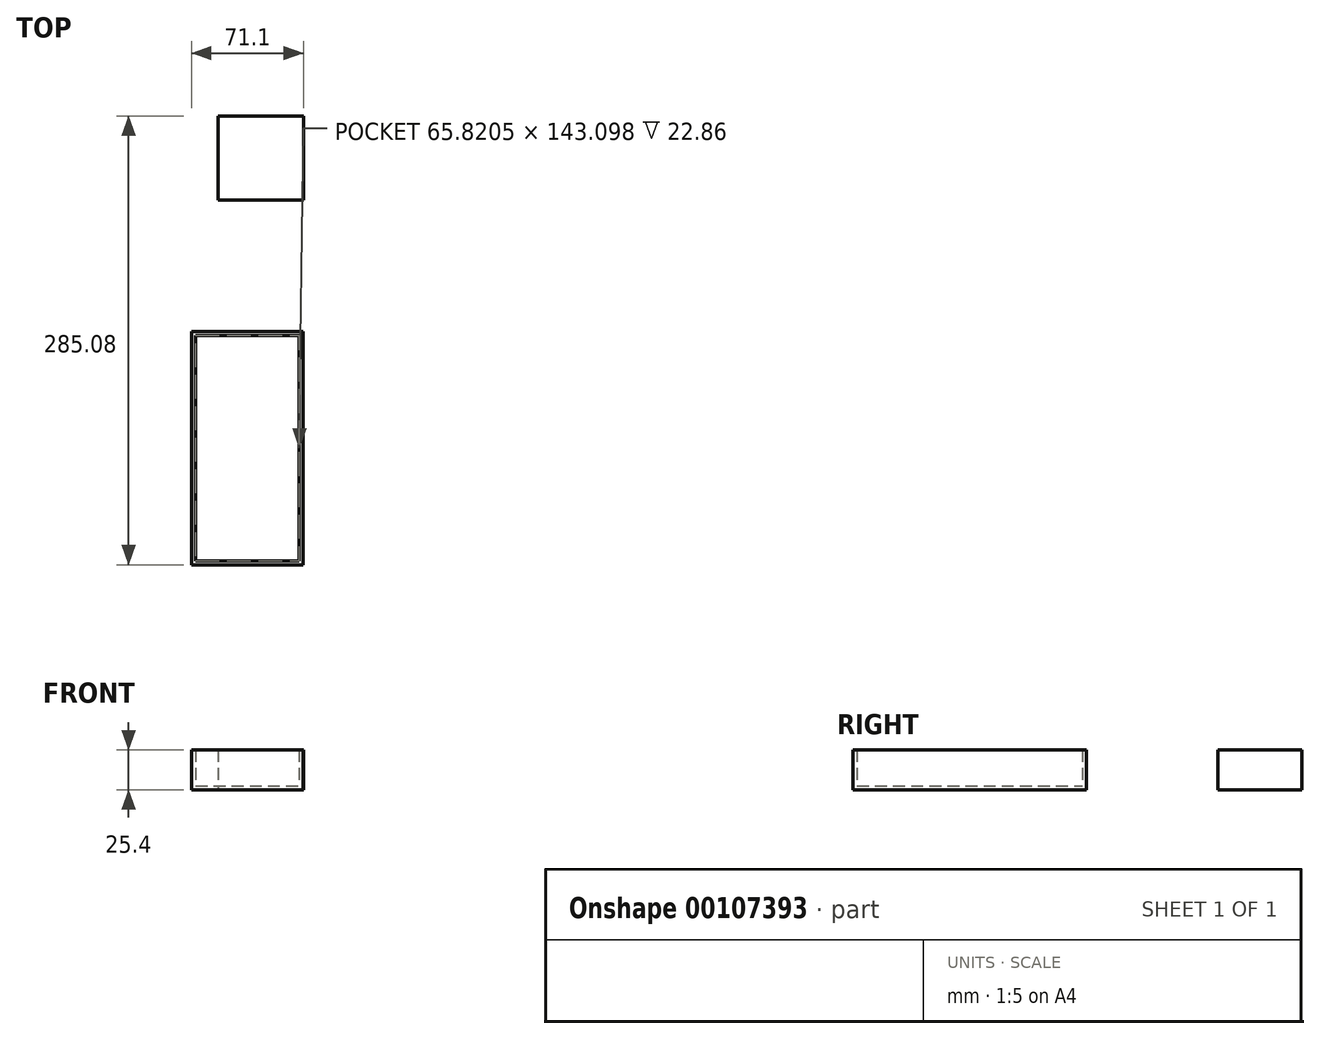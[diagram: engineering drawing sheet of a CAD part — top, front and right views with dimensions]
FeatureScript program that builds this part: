
annotation { "Feature Type Name" : "Feature", "Feature Type Description" : "" }
export const myFeature = defineFeature(function(context is Context, id is Id, definition is map)
    precondition{}
    {
        {
            var Q0;
            Q0=qCreatedBy(makeId("Top.planeOp"),FACE);
            var sketch = newSketch(context, id + "F0", { "sketchPlane" : qUnion([Q0])});
            skLineSegment(sketch, "E0.bottom", {"start": v(-3.03, -49.08) * mm, "end": v(57.44, -49.08) * mm});
            skLineSegment(sketch, "E0.top", {"start": v(-3.03, -82.84) * mm, "end": v(57.44, -82.84) * mm});
            skLineSegment(sketch, "E0.left", {"start": v(-3.03, -82.84) * mm, "end": v(-3.03, -49.08) * mm});
            skLineSegment(sketch, "E0.right", {"start": v(57.44, -82.84) * mm, "end": v(57.44, -49.08) * mm});
            skArc(sketch, "E1", {"start": v(57.44, -49.08) * mm, "mid": v(56.01, -65.96) * mm, "end": v(57.44, -82.84) * mm});
            skLineSegment(sketch, "E2.bottom", {"start": v(13.67, 34.55) * mm, "end": v(68.07, 34.55) * mm});
            skLineSegment(sketch, "E2.top", {"start": v(13.67, 87.83) * mm, "end": v(68.07, 87.83) * mm});
            skLineSegment(sketch, "E2.left", {"start": v(13.67, 34.55) * mm, "end": v(13.67, 87.83) * mm});
            skLineSegment(sketch, "E2.right", {"start": v(68.07, 34.55) * mm, "end": v(68.07, 87.83) * mm});
            skLineSegment(sketch, "E3", {"start": v(68.07, 87.83) * mm, "end": v(84.38, 37.67) * mm});
            skLineSegment(sketch, "E4", {"start": v(84.38, 37.67) * mm, "end": v(80.71, 0) * mm});
            skLineSegment(sketch, "E5.bottom", {"start": v(-3.03, -49.08) * mm, "end": v(67.87, -49.08) * mm});
            skLineSegment(sketch, "E5.top", {"start": v(-3.03, -197.25) * mm, "end": v(67.87, -197.25) * mm});
            skLineSegment(sketch, "E5.left", {"start": v(-3.03, -49.08) * mm, "end": v(-3.03, -197.25) * mm});
            skLineSegment(sketch, "E5.right", {"start": v(67.87, -49.08) * mm, "end": v(67.87, -197.25) * mm});
            skLineSegment(sketch, "E6", {"start": v(67.87, -197.25) * mm, "end": v(86.28, -173.38) * mm});
            skLineSegment(sketch, "E7", {"start": v(86.28, -173.38) * mm, "end": v(75.01, -124.74) * mm});
            skLineSegment(sketch, "E8", {"start": v(85.2, -173.38) * mm, "end": v(101.97, -58.45) * mm});
            skLineSegment(sketch, "E9", {"start": v(106.44, -67.94) * mm, "end": v(84.38, 37.67) * mm});
            skLineSegment(sketch, "E10", {"start": v(106.44, -67.94) * mm, "end": v(256.88, -65.96) * mm});
            skArc(sketch, "E11", {"start": v(13.67, 34.55) * mm, "mid": v(1.59, -6.52) * mm, "end": v(-3.03, -49.08) * mm});
            skSolve(sketch);
        }
        {
            var Q0;
            Q0 = qSketchRegion(id + "F0", true);
            extrude(context, id + "F1", {"entities" : qUnion([Q0]), "depth" : 25.4 * mm});
        }
        {
            var Q0;
            Q0=makeQuery(id+"F1.opExtrude","CAP_FACE",FACE,{"disambiguationData":[OSD([sQuery(id+"F0.wireOp",EDGE,"E0.top"),sQuery(id+"F0.wireOp",EDGE,"E0.left"),sQuery(id+"F0.wireOp",EDGE,"E0.right"),sQuery(id+"F0.wireOp",EDGE,"E1"),sQuery(id+"F0.wireOp",EDGE,"E2.top"),sQuery(id+"F0.wireOp",EDGE,"E2.left"),sQuery(id+"F0.wireOp",EDGE,"E3"),sQuery(id+"F0.wireOp",EDGE,"E5.top"),sQuery(id+"F0.wireOp",EDGE,"E5.left"),sQuery(id+"F0.wireOp",EDGE,"E6"),sQuery(id+"F0.wireOp",EDGE,"E7"),sQuery(id+"F0.wireOp",EDGE,"E8"),sQuery(id+"F0.wireOp",EDGE,"E9"),sQuery(id+"F0.wireOp",EDGE,"E10"),sQuery(id+"F0.wireOp",EDGE,"E11")])],"isStart":false});
            shell(context, id + "F2", {"entities" : qUnion([Q0]), "thickness" : 2.54 * mm});
        }
    });
